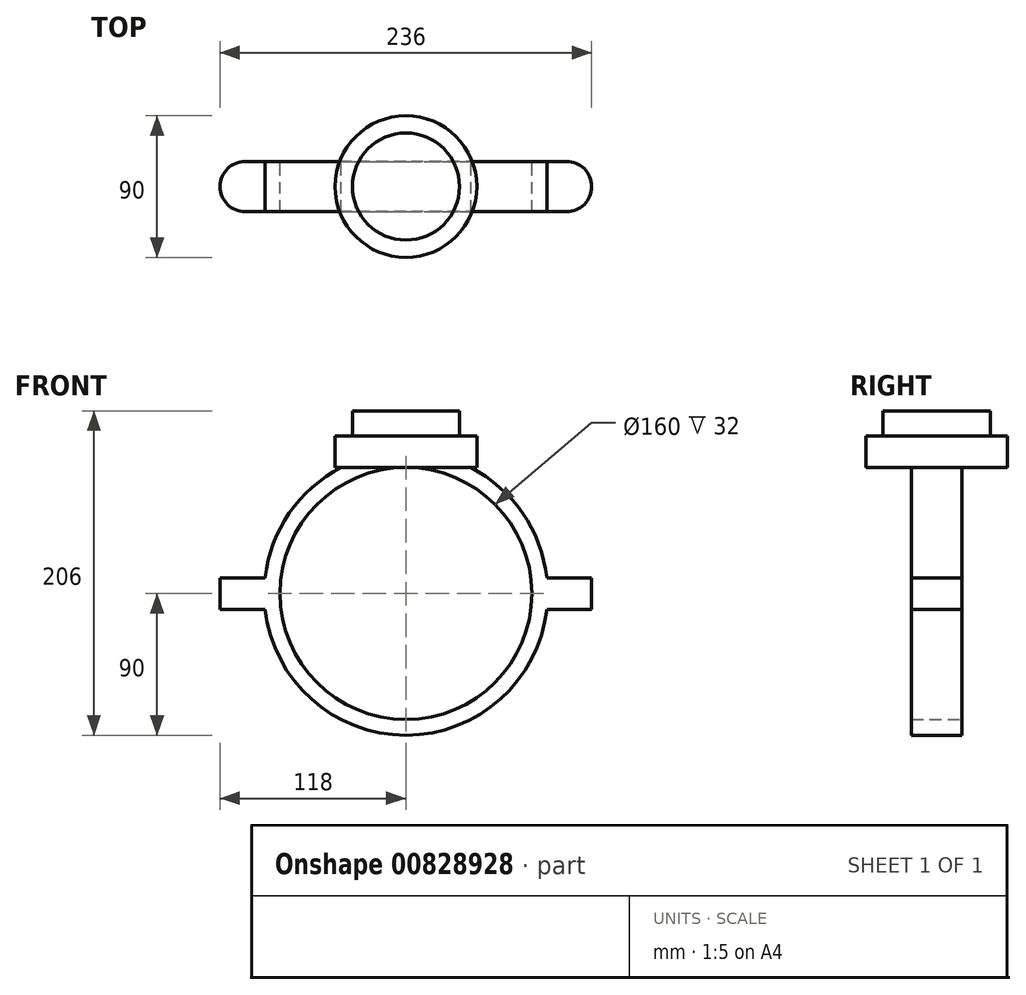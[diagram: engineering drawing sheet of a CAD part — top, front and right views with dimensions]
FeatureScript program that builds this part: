
annotation { "Feature Type Name" : "Feature", "Feature Type Description" : "" }
export const myFeature = defineFeature(function(context is Context, id is Id, definition is map)
    precondition{}
    {
        {
            var Q0;
            Q0=qCreatedBy(makeId("Front.planeOp"),FACE);
            var sketch = newSketch(context, id + "F0", { "sketchPlane" : qUnion([Q0])});
            skCircle(sketch, "E0", {"center": v(0, 0) * mm, "radius": 80 * mm});
            skCircle(sketch, "E1", {"center": v(0, 0) * mm, "radius": 90 * mm});
            skSolve(sketch);
        }
        {
            var Q0;
            Q0=makeQuery(id+"F0.imprint","IMPRINT",FACE,{"disambiguationData":[TD([[makeQuery(id+"F0.imprint","IMPRINT",EDGE,{"derivedFrom":sQuery(id+"F0.wireOp",EDGE,"E0")}),-1.0]])]});
            extrude(context, id + "F1", {"entities" : qUnion([Q0]), "endBound" : BoundingType.SYMMETRIC, "depth" : 32 * mm, "offsetDistance" : 25 * mm});
        }
        {
            var Q0;
            Q0=qCreatedBy(makeId("Right.planeOp"),FACE);
            var sketch = newSketch(context, id + "F2", { "sketchPlane" : qUnion([Q0])});
            skLineSegment(sketch, "E2", {"start": v(0, 0) * mm, "end": v(0, 80) * mm});
            skLineSegment(sketch, "E3", {"start": v(0, 80) * mm, "end": v(-45, 80) * mm});
            skLineSegment(sketch, "E4", {"start": v(-45, 80) * mm, "end": v(-45, 100) * mm});
            skLineSegment(sketch, "E5", {"start": v(-45, 100) * mm, "end": v(0, 100) * mm});
            skLineSegment(sketch, "E6", {"start": v(0, 100) * mm, "end": v(0, 116) * mm});
            skLineSegment(sketch, "E7", {"start": v(0, 116) * mm, "end": v(-34, 116) * mm});
            skLineSegment(sketch, "E8", {"start": v(-34, 116) * mm, "end": v(-34, 100) * mm});
            skLineSegment(sketch, "E9", {"start": v(0, 80) * mm, "end": v(0, 100) * mm});
            skSolve(sketch);
        }
        {
            var Q0;
            {var subQ0=sQuery(id+"F2.wireOp",EDGE,"E6");Q0=makeQuery(id+"F2.imprint","IMPRINT",FACE,{"disambiguationData":[TD([[makeQuery(id+"F2.imprint","IMPRINT",EDGE,{"derivedFrom":subQ0}),1.0]])]});}
            var Q1;
            Q1=makeQuery(id+"F2.imprint","IMPRINT",FACE,{"disambiguationData":[TD([[makeQuery(id+"F2.imprint","IMPRINT",EDGE,{"derivedFrom":sQuery(id+"F2.wireOp",EDGE,"E3")}),-1.0]])]});
            var Q2;
            Q2=sQuery(id+"F2.wireOp",EDGE,"E6");
            revolve(context, id + "F3", {"operationType" : NewBodyOperationType.ADD, "surfaceOperationType" : NewSurfaceOperationType.NEW, "entities" : qUnion([Q0, Q1]), "axis" : qUnion([Q2]), "revolveType" : RevolveType.FULL});
        }
        {
            var Q0;
            Q0=qCreatedBy(makeId("Top.planeOp"),FACE);
            var sketch = newSketch(context, id + "F4", { "sketchPlane" : qUnion([Q0])});
            skLineSegment(sketch, "E10", {"start": v(0, 0) * mm, "end": v(80, 0) * mm});
            skLineSegment(sketch, "E11", {"start": v(80, 0) * mm, "end": v(80, -16) * mm});
            skLineSegment(sketch, "E12", {"start": v(80, 0) * mm, "end": v(102, 0) * mm});
            skArc(sketch, "E13", {"start": v(102, -16) * mm, "mid": v(118, 0) * mm, "end": v(102, 16) * mm});
            skLineSegment(sketch, "E14", {"start": v(80, -16) * mm, "end": v(102, -16) * mm});
            skLineSegment(sketch, "E15", {"start": v(102, -16) * mm, "end": v(102, 16) * mm});
            skLineSegment(sketch, "E16", {"start": v(102, 16) * mm, "end": v(80, 16) * mm});
            skLineSegment(sketch, "E17", {"start": v(80, 16) * mm, "end": v(80, 0) * mm});
            skLineSegment(sketch, "E18", {"start": v(0, 0) * mm, "end": v(0, -25.87) * mm});
            skLineSegment(sketch, "E19.MirrorCS", {"start": v(-102, 16) * mm, "end": v(-80, 16) * mm});
            skArc(sketch, "E20.MirrorCS", {"start": v(-102, -16) * mm, "mid": v(-118, 0) * mm, "end": v(-102, 16) * mm});
            skLineSegment(sketch, "E21.MirrorCS", {"start": v(-80, -16) * mm, "end": v(-102, -16) * mm});
            skLineSegment(sketch, "E22.MirrorCS", {"start": v(-80, 0) * mm, "end": v(-80, -16) * mm});
            skLineSegment(sketch, "E23.MirrorCS", {"start": v(-80, 16) * mm, "end": v(-80, 0) * mm});
            skSolve(sketch);
        }
        {
            var Q0;
            Q0=makeQuery(id+"F4.imprint","IMPRINT",FACE,{"disambiguationData":[TD([[makeQuery(id+"F4.imprint","IMPRINT",EDGE,{"derivedFrom":sQuery(id+"F4.wireOp",EDGE,"E11")}),1.0]])]});
            var Q1;
            {var subQ0=sQuery(id+"F4.wireOp",EDGE,"E12");Q1=makeQuery(id+"F4.imprint","IMPRINT",FACE,{"disambiguationData":[TD([[makeQuery(id+"F4.imprint","IMPRINT",EDGE,{"derivedFrom":subQ0}),1.0]])]});}
            var Q2;
            {var subQ0=sQuery(id+"F4.wireOp",EDGE,"E13");Q2=makeQuery(id+"F4.imprint","IMPRINT",FACE,{"disambiguationData":[TD([[makeQuery(id+"F4.imprint","IMPRINT",EDGE,{"derivedFrom":subQ0}),1.0]])]});}
            var Q3;
            Q3=makeQuery(id+"F4.imprint","IMPRINT",FACE,{"disambiguationData":[TD([[makeQuery(id+"F4.imprint","IMPRINT",EDGE,{"derivedFrom":sQuery(id+"F4.wireOp",EDGE,"E19.MirrorCS")}),-1.0]])]});
            extrude(context, id + "F5", {"entities" : qUnion([Q0, Q1, Q2, Q3]), "operationType" : NewBodyOperationType.ADD, "endBound" : BoundingType.SYMMETRIC, "depth" : 20 * mm, "offsetDistance" : 25 * mm});
        }
    });
